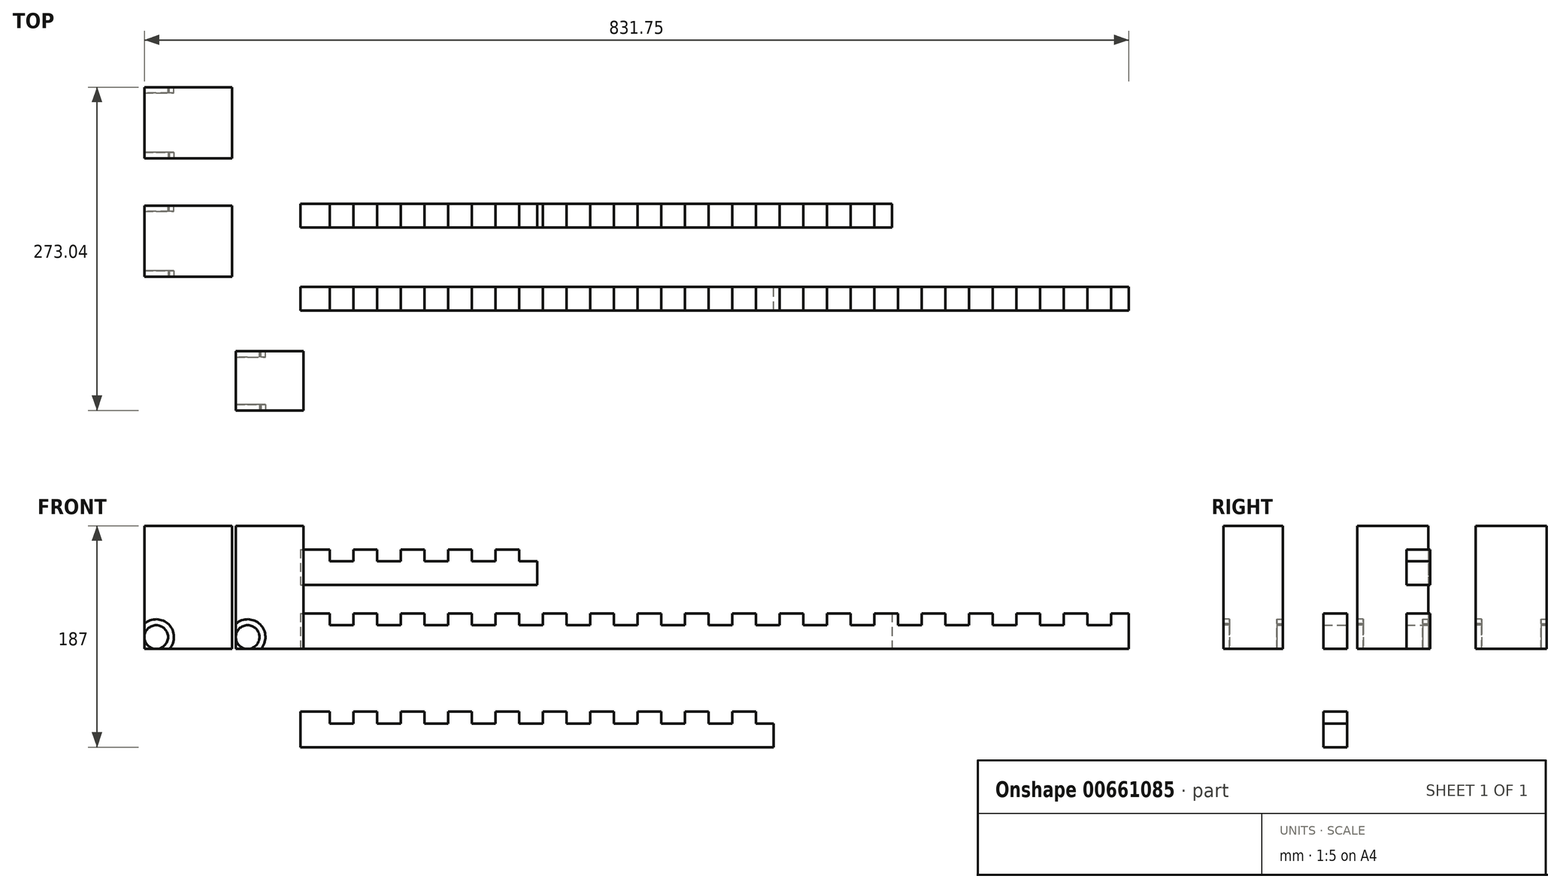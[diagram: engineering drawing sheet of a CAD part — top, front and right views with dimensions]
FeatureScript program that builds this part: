
annotation { "Feature Type Name" : "Feature", "Feature Type Description" : "" }
export const myFeature = defineFeature(function(context is Context, id is Id, definition is map)
    precondition{}
    {
        {
            var Q0;
            Q0=qCreatedBy(makeId("Top.planeOp"),FACE);
            var sketch = newSketch(context, id + "F0", { "sketchPlane" : qUnion([Q0])});
            skLineSegment(sketch, "E0.bottom", {"start": v(-131.75, 88.59) * mm, "end": v(-57.75, 88.59) * mm});
            skLineSegment(sketch, "E0.top", {"start": v(-131.75, 28.59) * mm, "end": v(-57.75, 28.59) * mm});
            skLineSegment(sketch, "E0.left", {"start": v(-131.75, 88.59) * mm, "end": v(-131.75, 28.59) * mm});
            skLineSegment(sketch, "E0.right", {"start": v(-57.75, 88.59) * mm, "end": v(-57.75, 28.59) * mm});
            skLineSegment(sketch, "E1.bottom", {"start": v(-54.5, -34.45) * mm, "end": v(2.5, -34.45) * mm});
            skLineSegment(sketch, "E1.top", {"start": v(-54.5, -84.45) * mm, "end": v(2.5, -84.45) * mm});
            skLineSegment(sketch, "E1.left", {"start": v(-54.5, -34.45) * mm, "end": v(-54.5, -84.45) * mm});
            skLineSegment(sketch, "E1.right", {"start": v(2.5, -34.45) * mm, "end": v(2.5, -84.45) * mm});
            skSolve(sketch);
        }
        {
            var Q0;
            Q0=makeQuery(id+"F0.imprint","IMPRINT",FACE,{"disambiguationData":[TD([[makeQuery(id+"F0.imprint","IMPRINT",EDGE,{"derivedFrom":sQuery(id+"F0.wireOp",EDGE,"E0.bottom")}),-1.0]])]});
            var Q1;
            Q1=makeQuery(id+"F0.imprint","IMPRINT",FACE,{"disambiguationData":[TD([[makeQuery(id+"F0.imprint","IMPRINT",EDGE,{"derivedFrom":sQuery(id+"F0.wireOp",EDGE,"E1.bottom")}),-1.0]])]});
            extrude(context, id + "F1", {"entities" : qUnion([Q0, Q1]), "depth" : 104 * mm, "offsetDistance" : 25 * mm});
        }
        {
            var Q0;
            Q0=makeQuery(id+"F1.opExtrude","SWEPT_FACE",FACE,{"disambiguationData":[OSD([sQuery(id+"F0.wireOp",EDGE,"E0.top")])]});
            var sketch = newSketch(context, id + "F2", { "sketchPlane" : qUnion([Q0])});
            skCircle(sketch, "E2", {"center": v(-121.75, 10) * mm, "radius": 10 * mm});
            skCircle(sketch, "E3", {"center": v(-121.75, 10) * mm, "radius": 15 * mm});
            skSolve(sketch);
        }
        {
            var Q0;
            {var subQ0=sQuery(id+"F2.wireOp",EDGE,"E2");var subQ1=sQuery(id+"F0.wireOp",EDGE,"E0.top");var subQ3=makeQuery(id+"F2.imprint","INTERSECT",VERTEX,{"derivedFrom":[makeQuery(id+"F1.opExtrude","CAP_EDGE",EDGE,{"disambiguationData":[OSD([subQ1])],"isStart":true}),subQ0]});Q0=makeQuery(id+"F2.imprint","IMPRINT",FACE,{"disambiguationData":[TD([[makeQuery(id+"F2.imprint","IMPRINT",EDGE,{"disambiguationData":[TD([[subQ3,1.0]])],"derivedFrom":subQ0}),1.0]])]});}
            extrude(context, id + "F3", {"entities" : qUnion([Q0]), "operationType" : NewBodyOperationType.ADD, "oppositeDirection" : true, "depth" : 5 * mm, "offsetDistance" : 25 * mm});
        }
        {
            var Q0;
            {var subQ1=sQuery(id+"F0.wireOp",EDGE,"E0.top");var subQ4=makeQuery(id+"F1.opExtrude","CAP_EDGE",EDGE,{"disambiguationData":[OSD([subQ1])],"isStart":true});var subQ6=sQuery(id+"F2.wireOp",EDGE,"E3");var subQ7=makeQuery(id+"F2.imprint","INTERSECT",VERTEX,{"derivedFrom":[subQ4,subQ6]});Q0=makeQuery(id+"F2.imprint","IMPRINT",FACE,{"disambiguationData":[TD([[makeQuery(id+"F2.imprint","IMPRINT",EDGE,{"disambiguationData":[TD([[subQ7,1.0]])],"derivedFrom":subQ4}),1.0]])]});}
            var Q1;
            {var subQ0=sQuery(id+"F0.wireOp",EDGE,"E0.top");var subQ1=makeQuery(id+"F1.opExtrude","CAP_EDGE",EDGE,{"disambiguationData":[OSD([subQ0])],"isStart":true});var subQ6=sQuery(id+"F2.wireOp",EDGE,"E3");var subQ9=makeQuery(id+"F2.imprint","INTERSECT",VERTEX,{"derivedFrom":[subQ1,subQ6]});Q1=makeQuery(id+"F2.imprint","IMPRINT",FACE,{"disambiguationData":[TD([[makeQuery(id+"F2.imprint","IMPRINT",EDGE,{"disambiguationData":[TD([[subQ9,1.0]])],"derivedFrom":subQ1}),-1.0]])]});}
            var Q2;
            {var subQ0=sQuery(id+"F2.wireOp",EDGE,"E2");var subQ1=sQuery(id+"F0.wireOp",EDGE,"E0.top");var subQ4=makeQuery(id+"F1.opExtrude","CAP_EDGE",EDGE,{"disambiguationData":[OSD([subQ1])],"isStart":true});var subQ5=makeQuery(id+"F2.imprint","INTERSECT",VERTEX,{"derivedFrom":[subQ4,subQ0]});Q2=makeQuery(id+"F2.imprint","IMPRINT",FACE,{"disambiguationData":[TD([[makeQuery(id+"F2.imprint","IMPRINT",EDGE,{"disambiguationData":[TD([[subQ5,1.0]])],"derivedFrom":subQ0}),-1.0]])]});}
            extrude(context, id + "F4", {"entities" : qUnion([Q0, Q1, Q2]), "operationType" : NewBodyOperationType.REMOVE, "oppositeDirection" : true, "depth" : 5 * mm, "offsetDistance" : 25 * mm});
        }
        {
            var Q0;
            Q0=makeQuery(id+"F1.opExtrude","SWEPT_FACE",FACE,{"disambiguationData":[OSD([sQuery(id+"F0.wireOp",EDGE,"E0.bottom")])]});
            var sketch = newSketch(context, id + "F5", { "sketchPlane" : qUnion([Q0])});
            skCircle(sketch, "E4", {"center": v(121.75, 10) * mm, "radius": 10 * mm});
            skCircle(sketch, "E5", {"center": v(121.75, 10) * mm, "radius": 15 * mm});
            skSolve(sketch);
        }
        {
            var Q0;
            {var subQ0=sQuery(id+"F5.wireOp",EDGE,"E4");var subQ1=sQuery(id+"F0.wireOp",EDGE,"E0.bottom");var subQ3=makeQuery(id+"F5.imprint","INTERSECT",VERTEX,{"derivedFrom":[makeQuery(id+"F1.opExtrude","CAP_EDGE",EDGE,{"disambiguationData":[OSD([subQ1])],"isStart":true}),subQ0]});Q0=makeQuery(id+"F5.imprint","IMPRINT",FACE,{"disambiguationData":[TD([[makeQuery(id+"F5.imprint","IMPRINT",EDGE,{"disambiguationData":[TD([[subQ3,1.0]])],"derivedFrom":subQ0}),1.0]])]});}
            extrude(context, id + "F6", {"entities" : qUnion([Q0]), "operationType" : NewBodyOperationType.ADD, "oppositeDirection" : true, "depth" : 5 * mm, "offsetDistance" : 25 * mm});
        }
        {
            var Q0;
            {var subQ0=sQuery(id+"F0.wireOp",EDGE,"E0.bottom");var subQ1=makeQuery(id+"F1.opExtrude","CAP_EDGE",EDGE,{"disambiguationData":[OSD([subQ0])],"isStart":true});var subQ7=sQuery(id+"F5.wireOp",EDGE,"E5");var subQ9=makeQuery(id+"F5.imprint","INTERSECT",VERTEX,{"derivedFrom":[subQ1,subQ7]});Q0=makeQuery(id+"F5.imprint","IMPRINT",FACE,{"disambiguationData":[TD([[makeQuery(id+"F5.imprint","IMPRINT",EDGE,{"disambiguationData":[TD([[subQ9,1.0]])],"derivedFrom":subQ1}),1.0]])]});}
            var Q1;
            {var subQ1=sQuery(id+"F0.wireOp",EDGE,"E0.bottom");var subQ4=makeQuery(id+"F1.opExtrude","CAP_EDGE",EDGE,{"disambiguationData":[OSD([subQ1])],"isStart":true});var subQ6=sQuery(id+"F5.wireOp",EDGE,"E5");var subQ8=makeQuery(id+"F5.imprint","INTERSECT",VERTEX,{"derivedFrom":[subQ4,subQ6]});Q1=makeQuery(id+"F5.imprint","IMPRINT",FACE,{"disambiguationData":[TD([[makeQuery(id+"F5.imprint","IMPRINT",EDGE,{"disambiguationData":[TD([[subQ8,1.0]])],"derivedFrom":subQ4}),-1.0]])]});}
            var Q2;
            {var subQ0=sQuery(id+"F5.wireOp",EDGE,"E4");var subQ1=sQuery(id+"F0.wireOp",EDGE,"E0.bottom");var subQ4=makeQuery(id+"F1.opExtrude","CAP_EDGE",EDGE,{"disambiguationData":[OSD([subQ1])],"isStart":true});var subQ5=makeQuery(id+"F5.imprint","INTERSECT",VERTEX,{"derivedFrom":[subQ4,subQ0]});Q2=makeQuery(id+"F5.imprint","IMPRINT",FACE,{"disambiguationData":[TD([[makeQuery(id+"F5.imprint","IMPRINT",EDGE,{"disambiguationData":[TD([[subQ5,-1.0]])],"derivedFrom":subQ0}),-1.0]])]});}
            extrude(context, id + "F7", {"entities" : qUnion([Q0, Q1, Q2]), "operationType" : NewBodyOperationType.REMOVE, "oppositeDirection" : true, "depth" : 5 * mm, "offsetDistance" : 25 * mm});
        }
        {
            var Q0;
            Q0=makeQuery(id+"F1.opExtrude","SWEPT_FACE",FACE,{"disambiguationData":[OSD([sQuery(id+"F0.wireOp",EDGE,"E1.top")])]});
            var sketch = newSketch(context, id + "F8", { "sketchPlane" : qUnion([Q0])});
            skCircle(sketch, "E6", {"center": v(-44.5, 10) * mm, "radius": 10 * mm});
            skCircle(sketch, "E7", {"center": v(-44.5, 10) * mm, "radius": 15 * mm});
            skSolve(sketch);
        }
        {
            var Q0;
            {var subQ0=sQuery(id+"F8.wireOp",EDGE,"E6");var subQ1=sQuery(id+"F0.wireOp",EDGE,"E1.top");var subQ3=makeQuery(id+"F8.imprint","INTERSECT",VERTEX,{"derivedFrom":[makeQuery(id+"F1.opExtrude","CAP_EDGE",EDGE,{"disambiguationData":[OSD([subQ1])],"isStart":true}),subQ0]});Q0=makeQuery(id+"F8.imprint","IMPRINT",FACE,{"disambiguationData":[TD([[makeQuery(id+"F8.imprint","IMPRINT",EDGE,{"disambiguationData":[TD([[subQ3,1.0]])],"derivedFrom":subQ0}),1.0]])]});}
            extrude(context, id + "F9", {"entities" : qUnion([Q0]), "operationType" : NewBodyOperationType.ADD, "oppositeDirection" : true, "depth" : 5 * mm, "offsetDistance" : 25 * mm});
        }
        {
            var Q0;
            {var subQ1=sQuery(id+"F0.wireOp",EDGE,"E1.top");var subQ4=makeQuery(id+"F1.opExtrude","CAP_EDGE",EDGE,{"disambiguationData":[OSD([subQ1])],"isStart":true});var subQ6=sQuery(id+"F8.wireOp",EDGE,"E7");var subQ7=makeQuery(id+"F8.imprint","INTERSECT",VERTEX,{"derivedFrom":[subQ4,subQ6]});Q0=makeQuery(id+"F8.imprint","IMPRINT",FACE,{"disambiguationData":[TD([[makeQuery(id+"F8.imprint","IMPRINT",EDGE,{"disambiguationData":[TD([[subQ7,1.0]])],"derivedFrom":subQ4}),1.0]])]});}
            var Q1;
            {var subQ0=sQuery(id+"F0.wireOp",EDGE,"E1.top");var subQ1=makeQuery(id+"F1.opExtrude","CAP_EDGE",EDGE,{"disambiguationData":[OSD([subQ0])],"isStart":true});var subQ6=sQuery(id+"F8.wireOp",EDGE,"E7");var subQ9=makeQuery(id+"F8.imprint","INTERSECT",VERTEX,{"derivedFrom":[subQ1,subQ6]});Q1=makeQuery(id+"F8.imprint","IMPRINT",FACE,{"disambiguationData":[TD([[makeQuery(id+"F8.imprint","IMPRINT",EDGE,{"disambiguationData":[TD([[subQ9,1.0]])],"derivedFrom":subQ1}),-1.0]])]});}
            var Q2;
            {var subQ0=sQuery(id+"F8.wireOp",EDGE,"E6");var subQ1=sQuery(id+"F0.wireOp",EDGE,"E1.top");var subQ4=makeQuery(id+"F1.opExtrude","CAP_EDGE",EDGE,{"disambiguationData":[OSD([subQ1])],"isStart":true});var subQ5=makeQuery(id+"F8.imprint","INTERSECT",VERTEX,{"derivedFrom":[subQ4,subQ0]});Q2=makeQuery(id+"F8.imprint","IMPRINT",FACE,{"disambiguationData":[TD([[makeQuery(id+"F8.imprint","IMPRINT",EDGE,{"disambiguationData":[TD([[subQ5,1.0]])],"derivedFrom":subQ0}),-1.0]])]});}
            extrude(context, id + "F10", {"entities" : qUnion([Q0, Q1, Q2]), "operationType" : NewBodyOperationType.REMOVE, "oppositeDirection" : true, "depth" : 5 * mm, "offsetDistance" : 25 * mm});
        }
        {
            var Q0;
            Q0=makeQuery(id+"F1.opExtrude","SWEPT_FACE",FACE,{"disambiguationData":[OSD([sQuery(id+"F0.wireOp",EDGE,"E1.bottom")])]});
            var sketch = newSketch(context, id + "F11", { "sketchPlane" : qUnion([Q0])});
            skCircle(sketch, "E8", {"center": v(44.5, 10) * mm, "radius": 10 * mm});
            skCircle(sketch, "E9", {"center": v(44.5, 10) * mm, "radius": 15 * mm});
            skSolve(sketch);
        }
        {
            var Q0;
            {var subQ0=sQuery(id+"F11.wireOp",EDGE,"E8");var subQ1=sQuery(id+"F0.wireOp",EDGE,"E1.bottom");var subQ3=makeQuery(id+"F11.imprint","INTERSECT",VERTEX,{"derivedFrom":[makeQuery(id+"F1.opExtrude","CAP_EDGE",EDGE,{"disambiguationData":[OSD([subQ1])],"isStart":true}),subQ0]});Q0=makeQuery(id+"F11.imprint","IMPRINT",FACE,{"disambiguationData":[TD([[makeQuery(id+"F11.imprint","IMPRINT",EDGE,{"disambiguationData":[TD([[subQ3,1.0]])],"derivedFrom":subQ0}),1.0]])]});}
            extrude(context, id + "F12", {"entities" : qUnion([Q0]), "operationType" : NewBodyOperationType.ADD, "oppositeDirection" : true, "depth" : 5 * mm, "offsetDistance" : 25 * mm});
        }
        {
            var Q0;
            {var subQ1=sQuery(id+"F0.wireOp",EDGE,"E1.bottom");var subQ4=makeQuery(id+"F1.opExtrude","CAP_EDGE",EDGE,{"disambiguationData":[OSD([subQ1])],"isStart":true});var subQ6=sQuery(id+"F11.wireOp",EDGE,"E9");var subQ8=makeQuery(id+"F11.imprint","INTERSECT",VERTEX,{"derivedFrom":[subQ4,subQ6]});Q0=makeQuery(id+"F11.imprint","IMPRINT",FACE,{"disambiguationData":[TD([[makeQuery(id+"F11.imprint","IMPRINT",EDGE,{"disambiguationData":[TD([[subQ8,1.0]])],"derivedFrom":subQ4}),-1.0]])]});}
            var Q1;
            {var subQ0=sQuery(id+"F11.wireOp",EDGE,"E8");var subQ1=sQuery(id+"F0.wireOp",EDGE,"E1.bottom");var subQ4=makeQuery(id+"F1.opExtrude","CAP_EDGE",EDGE,{"disambiguationData":[OSD([subQ1])],"isStart":true});var subQ5=makeQuery(id+"F11.imprint","INTERSECT",VERTEX,{"derivedFrom":[subQ4,subQ0]});Q1=makeQuery(id+"F11.imprint","IMPRINT",FACE,{"disambiguationData":[TD([[makeQuery(id+"F11.imprint","IMPRINT",EDGE,{"disambiguationData":[TD([[subQ5,-1.0]])],"derivedFrom":subQ0}),-1.0]])]});}
            extrude(context, id + "F13", {"entities" : qUnion([Q0, Q1]), "operationType" : NewBodyOperationType.REMOVE, "oppositeDirection" : true, "depth" : 5 * mm, "offsetDistance" : 25 * mm});
        }
        {
            var Q0;
            Q0=makeQuery(id+"F1.opExtrude","SWEPT_BODY",BODY,{"disambiguationData":[OSD([sQuery(id+"F0.wireOp",EDGE,"E0.bottom"),sQuery(id+"F0.wireOp",EDGE,"E0.top"),sQuery(id+"F0.wireOp",EDGE,"E0.left"),sQuery(id+"F0.wireOp",EDGE,"E0.right")])]});
            transform(context, id + "F14", {"entities" : qUnion([Q0]), "transformType" : TransformType.TRANSLATION_3D, "dx" : 0 * mm, "dy" : 0 * mm, "dz" : 0 * mm, "makeCopy" : true});
        }
        {
            var Q0;
            Q0=makeQuery(id+"F14.opPattern","COPY",BODY,{"derivedFrom":makeQuery(id+"F1.opExtrude","SWEPT_BODY",BODY,{"disambiguationData":[OSD([sQuery(id+"F0.wireOp",EDGE,"E0.bottom"),sQuery(id+"F0.wireOp",EDGE,"E0.top"),sQuery(id+"F0.wireOp",EDGE,"E0.left"),sQuery(id+"F0.wireOp",EDGE,"E0.right")])]}),"instanceName":"1"});
            deleteBodies(context, id + "F15", {"entities" : qUnion([Q0])});
        }
        {
            var Q0;
            Q0=makeQuery(id+"F1.opExtrude","SWEPT_BODY",BODY,{"disambiguationData":[OSD([sQuery(id+"F0.wireOp",EDGE,"E0.bottom"),sQuery(id+"F0.wireOp",EDGE,"E0.top"),sQuery(id+"F0.wireOp",EDGE,"E0.left"),sQuery(id+"F0.wireOp",EDGE,"E0.right")])]});
            transform(context, id + "F16", {"entities" : qUnion([Q0]), "transformType" : TransformType.TRANSLATION_3D, "dx" : 0 * mm, "dy" : 100 * mm, "dz" : 0 * mm, "makeCopy" : true});
        }
        {
            var Q0;
            Q0=qCreatedBy(makeId("Top.planeOp"),FACE);
            var sketch = newSketch(context, id + "F17", { "sketchPlane" : qUnion([Q0])});
            skLineSegment(sketch, "E10.bottom", {"start": v(0, 0) * mm, "end": v(700, 0) * mm});
            skLineSegment(sketch, "E10.top", {"start": v(0, 20) * mm, "end": v(700, 20) * mm});
            skLineSegment(sketch, "E10.left", {"start": v(0, 0) * mm, "end": v(0, 20) * mm});
            skLineSegment(sketch, "E10.right", {"start": v(700, 0) * mm, "end": v(700, 20) * mm});
            skSolve(sketch);
        }
        {
            var Q0;
            Q0=makeQuery(id+"F17.imprint","IMPRINT",FACE,{"disambiguationData":[TD([[makeQuery(id+"F17.imprint","IMPRINT",EDGE,{"derivedFrom":sQuery(id+"F17.wireOp",EDGE,"E10.bottom")}),1.0]])]});
            extrude(context, id + "F18", {"entities" : qUnion([Q0]), "depth" : 30 * mm, "offsetDistance" : 25 * mm});
        }
        {
            var Q0;
            Q0=makeQuery(id+"F18.opExtrude","SWEPT_FACE",FACE,{"disambiguationData":[OSD([sQuery(id+"F17.wireOp",EDGE,"E10.top")])]});
            var sketch = newSketch(context, id + "F19", { "sketchPlane" : qUnion([Q0])});
            skLineSegment(sketch, "E11.bottom", {"start": v(-684.9, 30) * mm, "end": v(-664.9, 30) * mm});
            skLineSegment(sketch, "E11.top", {"start": v(-684.9, 20) * mm, "end": v(-664.9, 20) * mm});
            skLineSegment(sketch, "E11.left", {"start": v(-684.9, 30) * mm, "end": v(-684.9, 20) * mm});
            skLineSegment(sketch, "E11.right", {"start": v(-664.9, 30) * mm, "end": v(-664.9, 20) * mm});
            skLineSegment(sketch, "E12.1.0.0", {"start": v(-644.9, 20) * mm, "end": v(-624.9, 20) * mm});
            skLineSegment(sketch, "E12.1.0.1", {"start": v(-644.9, 30) * mm, "end": v(-624.9, 30) * mm});
            skLineSegment(sketch, "E12.1.0.2", {"start": v(-644.9, 30) * mm, "end": v(-644.9, 20) * mm});
            skLineSegment(sketch, "E12.1.0.3", {"start": v(-624.9, 30) * mm, "end": v(-624.9, 20) * mm});
            skLineSegment(sketch, "E12.2.0.0", {"start": v(-604.9, 20) * mm, "end": v(-584.9, 20) * mm});
            skLineSegment(sketch, "E12.2.0.1", {"start": v(-604.9, 30) * mm, "end": v(-584.9, 30) * mm});
            skLineSegment(sketch, "E12.2.0.2", {"start": v(-604.9, 30) * mm, "end": v(-604.9, 20) * mm});
            skLineSegment(sketch, "E12.2.0.3", {"start": v(-584.9, 30) * mm, "end": v(-584.9, 20) * mm});
            skLineSegment(sketch, "E12.3.0.0", {"start": v(-564.9, 20) * mm, "end": v(-544.9, 20) * mm});
            skLineSegment(sketch, "E12.3.0.1", {"start": v(-564.9, 30) * mm, "end": v(-544.9, 30) * mm});
            skLineSegment(sketch, "E12.3.0.2", {"start": v(-564.9, 30) * mm, "end": v(-564.9, 20) * mm});
            skLineSegment(sketch, "E12.3.0.3", {"start": v(-544.9, 30) * mm, "end": v(-544.9, 20) * mm});
            skLineSegment(sketch, "E12.4.0.0", {"start": v(-524.9, 20) * mm, "end": v(-504.9, 20) * mm});
            skLineSegment(sketch, "E12.4.0.1", {"start": v(-524.9, 30) * mm, "end": v(-504.9, 30) * mm});
            skLineSegment(sketch, "E12.4.0.2", {"start": v(-524.9, 30) * mm, "end": v(-524.9, 20) * mm});
            skLineSegment(sketch, "E12.4.0.3", {"start": v(-504.9, 30) * mm, "end": v(-504.9, 20) * mm});
            skLineSegment(sketch, "E12.5.0.0", {"start": v(-484.9, 20) * mm, "end": v(-464.9, 20) * mm});
            skLineSegment(sketch, "E12.5.0.1", {"start": v(-484.9, 30) * mm, "end": v(-464.9, 30) * mm});
            skLineSegment(sketch, "E12.5.0.2", {"start": v(-484.9, 30) * mm, "end": v(-484.9, 20) * mm});
            skLineSegment(sketch, "E12.5.0.3", {"start": v(-464.9, 30) * mm, "end": v(-464.9, 20) * mm});
            skLineSegment(sketch, "E12.6.0.0", {"start": v(-444.9, 20) * mm, "end": v(-424.9, 20) * mm});
            skLineSegment(sketch, "E12.6.0.1", {"start": v(-444.9, 30) * mm, "end": v(-424.9, 30) * mm});
            skLineSegment(sketch, "E12.6.0.2", {"start": v(-444.9, 30) * mm, "end": v(-444.9, 20) * mm});
            skLineSegment(sketch, "E12.6.0.3", {"start": v(-424.9, 30) * mm, "end": v(-424.9, 20) * mm});
            skLineSegment(sketch, "E12.7.0.0", {"start": v(-404.9, 20) * mm, "end": v(-384.9, 20) * mm});
            skLineSegment(sketch, "E12.7.0.1", {"start": v(-404.9, 30) * mm, "end": v(-384.9, 30) * mm});
            skLineSegment(sketch, "E12.7.0.2", {"start": v(-404.9, 30) * mm, "end": v(-404.9, 20) * mm});
            skLineSegment(sketch, "E12.7.0.3", {"start": v(-384.9, 30) * mm, "end": v(-384.9, 20) * mm});
            skLineSegment(sketch, "E12.8.0.0", {"start": v(-364.9, 20) * mm, "end": v(-344.9, 20) * mm});
            skLineSegment(sketch, "E12.8.0.1", {"start": v(-364.9, 30) * mm, "end": v(-344.9, 30) * mm});
            skLineSegment(sketch, "E12.8.0.2", {"start": v(-364.9, 30) * mm, "end": v(-364.9, 20) * mm});
            skLineSegment(sketch, "E12.8.0.3", {"start": v(-344.9, 30) * mm, "end": v(-344.9, 20) * mm});
            skLineSegment(sketch, "E12.9.0.0", {"start": v(-324.9, 20) * mm, "end": v(-304.9, 20) * mm});
            skLineSegment(sketch, "E12.9.0.1", {"start": v(-324.9, 30) * mm, "end": v(-304.9, 30) * mm});
            skLineSegment(sketch, "E12.9.0.2", {"start": v(-324.9, 30) * mm, "end": v(-324.9, 20) * mm});
            skLineSegment(sketch, "E12.9.0.3", {"start": v(-304.9, 30) * mm, "end": v(-304.9, 20) * mm});
            skLineSegment(sketch, "E12.10.0.0", {"start": v(-284.9, 20) * mm, "end": v(-264.9, 20) * mm});
            skLineSegment(sketch, "E12.10.0.1", {"start": v(-284.9, 30) * mm, "end": v(-264.9, 30) * mm});
            skLineSegment(sketch, "E12.10.0.2", {"start": v(-284.9, 30) * mm, "end": v(-284.9, 20) * mm});
            skLineSegment(sketch, "E12.10.0.3", {"start": v(-264.9, 30) * mm, "end": v(-264.9, 20) * mm});
            skLineSegment(sketch, "E12.11.0.0", {"start": v(-244.9, 20) * mm, "end": v(-224.9, 20) * mm});
            skLineSegment(sketch, "E12.11.0.1", {"start": v(-244.9, 30) * mm, "end": v(-224.9, 30) * mm});
            skLineSegment(sketch, "E12.11.0.2", {"start": v(-244.9, 30) * mm, "end": v(-244.9, 20) * mm});
            skLineSegment(sketch, "E12.11.0.3", {"start": v(-224.9, 30) * mm, "end": v(-224.9, 20) * mm});
            skLineSegment(sketch, "E12.12.0.0", {"start": v(-204.9, 20) * mm, "end": v(-184.9, 20) * mm});
            skLineSegment(sketch, "E12.12.0.1", {"start": v(-204.9, 30) * mm, "end": v(-184.9, 30) * mm});
            skLineSegment(sketch, "E12.12.0.2", {"start": v(-204.9, 30) * mm, "end": v(-204.9, 20) * mm});
            skLineSegment(sketch, "E12.12.0.3", {"start": v(-184.9, 30) * mm, "end": v(-184.9, 20) * mm});
            skLineSegment(sketch, "E12.13.0.0", {"start": v(-164.9, 20) * mm, "end": v(-144.9, 20) * mm});
            skLineSegment(sketch, "E12.13.0.1", {"start": v(-164.9, 30) * mm, "end": v(-144.9, 30) * mm});
            skLineSegment(sketch, "E12.13.0.2", {"start": v(-164.9, 30) * mm, "end": v(-164.9, 20) * mm});
            skLineSegment(sketch, "E12.13.0.3", {"start": v(-144.9, 30) * mm, "end": v(-144.9, 20) * mm});
            skLineSegment(sketch, "E12.14.0.0", {"start": v(-124.9, 20) * mm, "end": v(-104.9, 20) * mm});
            skLineSegment(sketch, "E12.14.0.1", {"start": v(-124.9, 30) * mm, "end": v(-104.9, 30) * mm});
            skLineSegment(sketch, "E12.14.0.2", {"start": v(-124.9, 30) * mm, "end": v(-124.9, 20) * mm});
            skLineSegment(sketch, "E12.14.0.3", {"start": v(-104.9, 30) * mm, "end": v(-104.9, 20) * mm});
            skLineSegment(sketch, "E12.15.0.0", {"start": v(-84.9, 20) * mm, "end": v(-64.9, 20) * mm});
            skLineSegment(sketch, "E12.15.0.1", {"start": v(-84.9, 30) * mm, "end": v(-64.9, 30) * mm});
            skLineSegment(sketch, "E12.15.0.2", {"start": v(-84.9, 30) * mm, "end": v(-84.9, 20) * mm});
            skLineSegment(sketch, "E12.15.0.3", {"start": v(-64.9, 30) * mm, "end": v(-64.9, 20) * mm});
            skLineSegment(sketch, "E12.16.0.0", {"start": v(-44.9, 20) * mm, "end": v(-24.9, 20) * mm});
            skLineSegment(sketch, "E12.16.0.1", {"start": v(-44.9, 30) * mm, "end": v(-24.9, 30) * mm});
            skLineSegment(sketch, "E12.16.0.2", {"start": v(-44.9, 30) * mm, "end": v(-44.9, 20) * mm});
            skLineSegment(sketch, "E12.16.0.3", {"start": v(-24.9, 30) * mm, "end": v(-24.9, 20) * mm});
            skLineSegment(sketch, "E12.direction1", {"start": v(-684.9, 20) * mm, "end": v(-644.9, 20) * mm, "construction": true});
            skSolve(sketch);
        }
        {
            var Q0;
            Q0=makeQuery(id+"F19.imprint","IMPRINT",FACE,{"disambiguationData":[TD([[makeQuery(id+"F19.imprint","IMPRINT",EDGE,{"derivedFrom":sQuery(id+"F19.wireOp",EDGE,"E11.bottom")}),1.0]])]});
            var Q1;
            Q1=makeQuery(id+"F19.imprint","IMPRINT",FACE,{"disambiguationData":[TD([[makeQuery(id+"F19.imprint","IMPRINT",EDGE,{"derivedFrom":sQuery(id+"F19.wireOp",EDGE,"E12.1.0.0")}),1.0]])]});
            var Q2;
            Q2=makeQuery(id+"F19.imprint","IMPRINT",FACE,{"disambiguationData":[TD([[makeQuery(id+"F19.imprint","IMPRINT",EDGE,{"derivedFrom":sQuery(id+"F19.wireOp",EDGE,"E12.2.0.0")}),1.0]])]});
            var Q3;
            Q3=makeQuery(id+"F19.imprint","IMPRINT",FACE,{"disambiguationData":[TD([[makeQuery(id+"F19.imprint","IMPRINT",EDGE,{"derivedFrom":sQuery(id+"F19.wireOp",EDGE,"E12.3.0.0")}),1.0]])]});
            var Q4;
            Q4=makeQuery(id+"F19.imprint","IMPRINT",FACE,{"disambiguationData":[TD([[makeQuery(id+"F19.imprint","IMPRINT",EDGE,{"derivedFrom":sQuery(id+"F19.wireOp",EDGE,"E12.4.0.0")}),1.0]])]});
            var Q5;
            Q5=makeQuery(id+"F19.imprint","IMPRINT",FACE,{"disambiguationData":[TD([[makeQuery(id+"F19.imprint","IMPRINT",EDGE,{"derivedFrom":sQuery(id+"F19.wireOp",EDGE,"E12.5.0.0")}),1.0]])]});
            var Q6;
            Q6=makeQuery(id+"F19.imprint","IMPRINT",FACE,{"disambiguationData":[TD([[makeQuery(id+"F19.imprint","IMPRINT",EDGE,{"derivedFrom":sQuery(id+"F19.wireOp",EDGE,"E12.6.0.0")}),1.0]])]});
            var Q7;
            Q7=makeQuery(id+"F19.imprint","IMPRINT",FACE,{"disambiguationData":[TD([[makeQuery(id+"F19.imprint","IMPRINT",EDGE,{"derivedFrom":sQuery(id+"F19.wireOp",EDGE,"E12.7.0.0")}),1.0]])]});
            var Q8;
            Q8=makeQuery(id+"F19.imprint","IMPRINT",FACE,{"disambiguationData":[TD([[makeQuery(id+"F19.imprint","IMPRINT",EDGE,{"derivedFrom":sQuery(id+"F19.wireOp",EDGE,"E12.8.0.0")}),1.0]])]});
            var Q9;
            Q9=makeQuery(id+"F19.imprint","IMPRINT",FACE,{"disambiguationData":[TD([[makeQuery(id+"F19.imprint","IMPRINT",EDGE,{"derivedFrom":sQuery(id+"F19.wireOp",EDGE,"E12.9.0.0")}),1.0]])]});
            var Q10;
            Q10=makeQuery(id+"F19.imprint","IMPRINT",FACE,{"disambiguationData":[TD([[makeQuery(id+"F19.imprint","IMPRINT",EDGE,{"derivedFrom":sQuery(id+"F19.wireOp",EDGE,"E12.10.0.0")}),1.0]])]});
            var Q11;
            Q11=makeQuery(id+"F19.imprint","IMPRINT",FACE,{"disambiguationData":[TD([[makeQuery(id+"F19.imprint","IMPRINT",EDGE,{"derivedFrom":sQuery(id+"F19.wireOp",EDGE,"E12.11.0.0")}),1.0]])]});
            var Q12;
            Q12=makeQuery(id+"F19.imprint","IMPRINT",FACE,{"disambiguationData":[TD([[makeQuery(id+"F19.imprint","IMPRINT",EDGE,{"derivedFrom":sQuery(id+"F19.wireOp",EDGE,"E12.12.0.0")}),1.0]])]});
            var Q13;
            Q13=makeQuery(id+"F19.imprint","IMPRINT",FACE,{"disambiguationData":[TD([[makeQuery(id+"F19.imprint","IMPRINT",EDGE,{"derivedFrom":sQuery(id+"F19.wireOp",EDGE,"E12.13.0.0")}),1.0]])]});
            var Q14;
            Q14=makeQuery(id+"F19.imprint","IMPRINT",FACE,{"disambiguationData":[TD([[makeQuery(id+"F19.imprint","IMPRINT",EDGE,{"derivedFrom":sQuery(id+"F19.wireOp",EDGE,"E12.14.0.0")}),1.0]])]});
            var Q15;
            Q15=makeQuery(id+"F19.imprint","IMPRINT",FACE,{"disambiguationData":[TD([[makeQuery(id+"F19.imprint","IMPRINT",EDGE,{"derivedFrom":sQuery(id+"F19.wireOp",EDGE,"E12.15.0.0")}),1.0]])]});
            var Q16;
            Q16=makeQuery(id+"F19.imprint","IMPRINT",FACE,{"disambiguationData":[TD([[makeQuery(id+"F19.imprint","IMPRINT",EDGE,{"derivedFrom":sQuery(id+"F19.wireOp",EDGE,"E12.16.0.0")}),1.0]])]});
            extrude(context, id + "F20", {"entities" : qUnion([Q0, Q1, Q2, Q3, Q4, Q5, Q6, Q7, Q8, Q9, Q10, Q11, Q12, Q13, Q14, Q15, Q16]), "operationType" : NewBodyOperationType.REMOVE, "oppositeDirection" : true, "depth" : 25 * mm, "offsetDistance" : 25 * mm});
        }
        {
            var Q0;
            Q0=makeQuery(id+"F18.opExtrude","SWEPT_BODY",BODY,{"disambiguationData":[OSD([sQuery(id+"F17.wireOp",EDGE,"E10.bottom"),sQuery(id+"F17.wireOp",EDGE,"E10.top"),sQuery(id+"F17.wireOp",EDGE,"E10.left"),sQuery(id+"F17.wireOp",EDGE,"E10.right")])]});
            transform(context, id + "F21", {"entities" : qUnion([Q0]), "transformType" : TransformType.TRANSLATION_3D, "dx" : 0 * mm, "dy" : 70 * mm, "dz" : 0 * mm, "makeCopy" : true});
        }
        {
            var Q0;
            Q0=makeQuery(id+"F21.opPattern","COPY",FACE,{"derivedFrom":makeQuery(id+"F18.opExtrude","SWEPT_FACE",FACE,{"disambiguationData":[OSD([sQuery(id+"F17.wireOp",EDGE,"E10.right")])]}),"instanceName":"1"});
            var sketch = newSketch(context, id + "F22", { "sketchPlane" : qUnion([Q0])});
            skLineSegment(sketch, "E13.bottom", {"start": v(70, 30) * mm, "end": v(90, 30) * mm});
            skLineSegment(sketch, "E13.top", {"start": v(70, 0) * mm, "end": v(90, 0) * mm});
            skLineSegment(sketch, "E13.left", {"start": v(70, 30) * mm, "end": v(70, 0) * mm});
            skLineSegment(sketch, "E13.right", {"start": v(90, 30) * mm, "end": v(90, 0) * mm});
            skSolve(sketch);
        }
        {
            var Q0;
            Q0=makeQuery(id+"F22.imprint","IMPRINT",FACE,{"disambiguationData":[TD([[makeQuery(id+"F22.imprint","IMPRINT",EDGE,{"derivedFrom":sQuery(id+"F22.wireOp",EDGE,"E13.bottom")}),-1.0]])]});
            extrude(context, id + "F23", {"entities" : qUnion([Q0]), "operationType" : NewBodyOperationType.REMOVE, "oppositeDirection" : true, "depth" : 200 * mm, "offsetDistance" : 25 * mm});
        }
        {
            var Q0;
            Q0=makeQuery(id+"F18.opExtrude","SWEPT_BODY",BODY,{"disambiguationData":[OSD([sQuery(id+"F17.wireOp",EDGE,"E10.bottom"),sQuery(id+"F17.wireOp",EDGE,"E10.top"),sQuery(id+"F17.wireOp",EDGE,"E10.left"),sQuery(id+"F17.wireOp",EDGE,"E10.right")])]});
            transform(context, id + "F24", {"entities" : qUnion([Q0]), "transformType" : TransformType.TRANSLATION_3D, "dx" : 0 * mm, "dy" : 0 * mm, "dz" : -83 * mm, "makeCopy" : true});
        }
        {
            var Q0;
            Q0=makeQuery(id+"F21.opPattern","COPY",BODY,{"derivedFrom":makeQuery(id+"F18.opExtrude","SWEPT_BODY",BODY,{"disambiguationData":[OSD([sQuery(id+"F17.wireOp",EDGE,"E10.bottom"),sQuery(id+"F17.wireOp",EDGE,"E10.top"),sQuery(id+"F17.wireOp",EDGE,"E10.left"),sQuery(id+"F17.wireOp",EDGE,"E10.right")])]}),"instanceName":"1"});
            transform(context, id + "F25", {"entities" : qUnion([Q0]), "transformType" : TransformType.TRANSLATION_3D, "dx" : 0 * mm, "dy" : 0 * mm, "dz" : 54 * mm, "makeCopy" : true});
        }
        {
            var Q0;
            Q0=makeQuery(id+"F25.opPattern","COPY",FACE,{"derivedFrom":makeQuery(id+"F23.boolean.opBoolean","COPY",FACE,{"derivedFrom":makeQuery(id+"F23.opExtrude","CAP_FACE",FACE,{"disambiguationData":[OSD([sQuery(id+"F22.wireOp",EDGE,"E13.bottom"),sQuery(id+"F22.wireOp",EDGE,"E13.top"),sQuery(id+"F22.wireOp",EDGE,"E13.left"),sQuery(id+"F22.wireOp",EDGE,"E13.right")])],"isStart":false})}),"instanceName":"1"});
            var sketch = newSketch(context, id + "F26", { "sketchPlane" : qUnion([Q0])});
            skLineSegment(sketch, "E14.bottom", {"start": v(70, 84) * mm, "end": v(90, 84) * mm});
            skLineSegment(sketch, "E14.top", {"start": v(70, 54) * mm, "end": v(90, 54) * mm});
            skLineSegment(sketch, "E14.left", {"start": v(70, 84) * mm, "end": v(70, 54) * mm});
            skLineSegment(sketch, "E14.right", {"start": v(90, 84) * mm, "end": v(90, 54) * mm});
            skSolve(sketch);
        }
        {
            var Q0;
            Q0=makeQuery(id+"F26.imprint","IMPRINT",FACE,{"disambiguationData":[TD([[makeQuery(id+"F26.imprint","IMPRINT",EDGE,{"derivedFrom":sQuery(id+"F26.wireOp",EDGE,"E14.bottom")}),-1.0]])]});
            extrude(context, id + "F27", {"entities" : qUnion([Q0]), "operationType" : NewBodyOperationType.REMOVE, "oppositeDirection" : true, "depth" : 300 * mm, "offsetDistance" : 25 * mm});
        }
        {
            var Q0;
            Q0=makeQuery(id+"F24.opPattern","COPY",FACE,{"derivedFrom":makeQuery(id+"F18.opExtrude","SWEPT_FACE",FACE,{"disambiguationData":[OSD([sQuery(id+"F17.wireOp",EDGE,"E10.right")])]}),"instanceName":"1"});
            var sketch = newSketch(context, id + "F28", { "sketchPlane" : qUnion([Q0])});
            skLineSegment(sketch, "E15.bottom", {"start": v(0, -53) * mm, "end": v(20, -53) * mm});
            skLineSegment(sketch, "E15.top", {"start": v(0, -83) * mm, "end": v(20, -83) * mm});
            skLineSegment(sketch, "E15.left", {"start": v(0, -53) * mm, "end": v(0, -83) * mm});
            skLineSegment(sketch, "E15.right", {"start": v(20, -53) * mm, "end": v(20, -83) * mm});
            skSolve(sketch);
        }
        {
            var Q0;
            Q0=makeQuery(id+"F28.imprint","IMPRINT",FACE,{"disambiguationData":[TD([[makeQuery(id+"F28.imprint","IMPRINT",EDGE,{"derivedFrom":sQuery(id+"F28.wireOp",EDGE,"E15.bottom")}),-1.0]])]});
            extrude(context, id + "F29", {"entities" : qUnion([Q0]), "operationType" : NewBodyOperationType.REMOVE, "oppositeDirection" : true, "depth" : 300 * mm, "offsetDistance" : 25 * mm});
        }
    });
